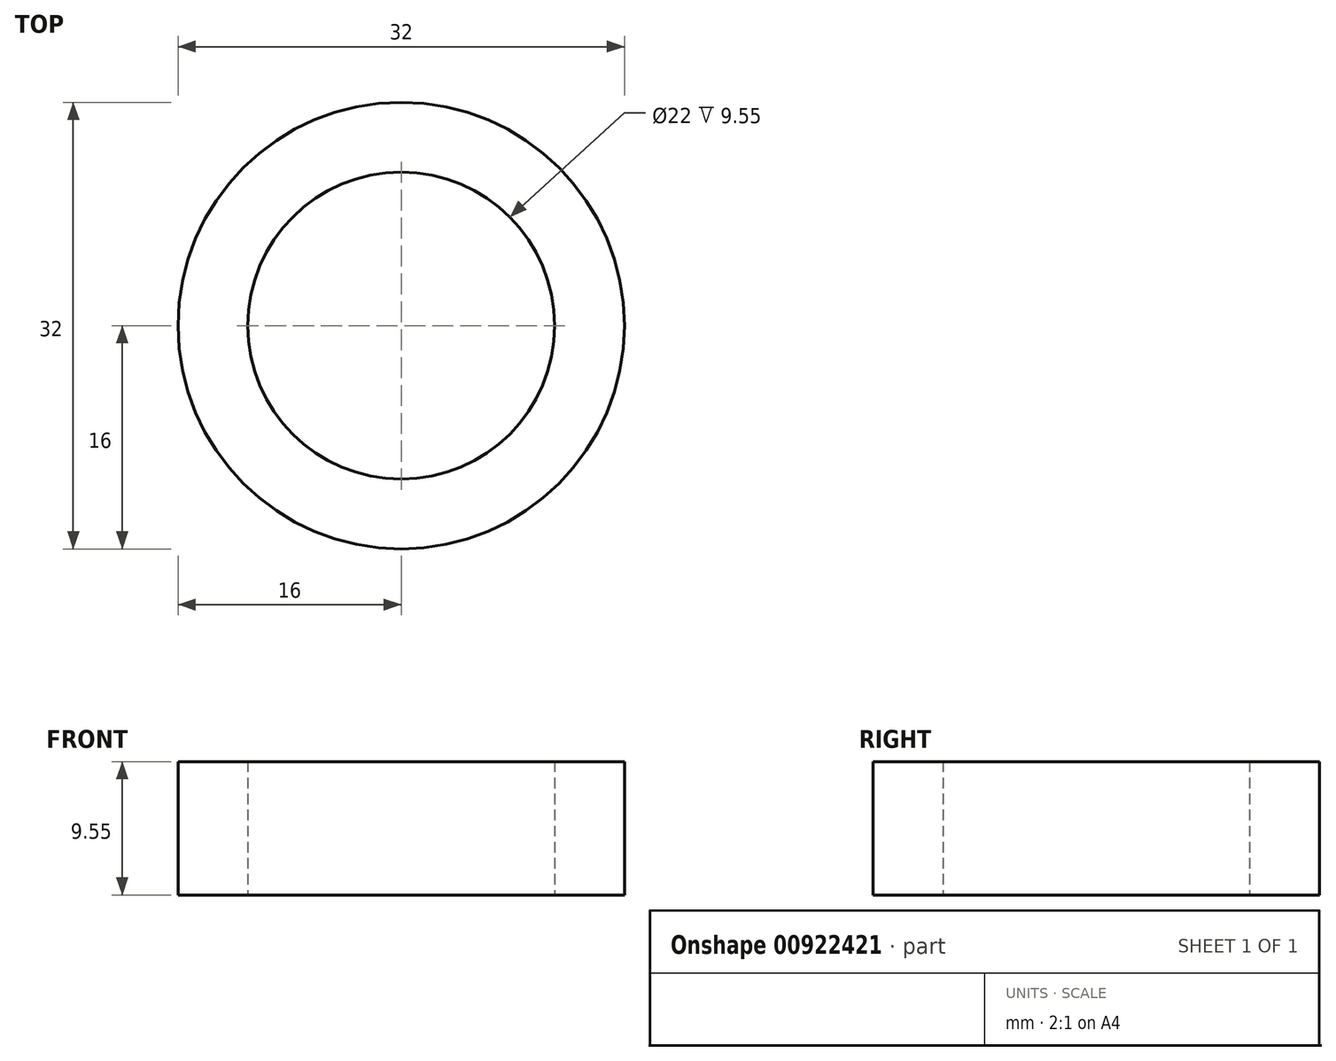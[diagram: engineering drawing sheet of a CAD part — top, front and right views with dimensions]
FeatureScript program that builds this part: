
annotation { "Feature Type Name" : "Feature", "Feature Type Description" : "" }
export const myFeature = defineFeature(function(context is Context, id is Id, definition is map)
    precondition{}
    {
        {
            var Q0;
            Q0=qCreatedBy(makeId("Top.planeOp"),FACE);
            var sketch = newSketch(context, id + "F0", { "sketchPlane" : qUnion([Q0])});
            skCircle(sketch, "E0", {"center": v(0, 0) * mm, "radius": 11 * mm});
            skCircle(sketch, "E1", {"center": v(0, 0) * mm, "radius": 16 * mm});
            skSolve(sketch);
        }
        {
            var Q0;
            Q0=makeQuery(id+"F0.imprint","IMPRINT",FACE,{"disambiguationData":[TD([[makeQuery(id+"F0.imprint","IMPRINT",EDGE,{"derivedFrom":sQuery(id+"F0.wireOp",EDGE,"E0")}),-1.0]])]});
            extrude(context, id + "F1", {"entities" : qUnion([Q0]), "depth" : 9.55 * mm, "offsetDistance" : 25.4 * mm});
        }
    });
